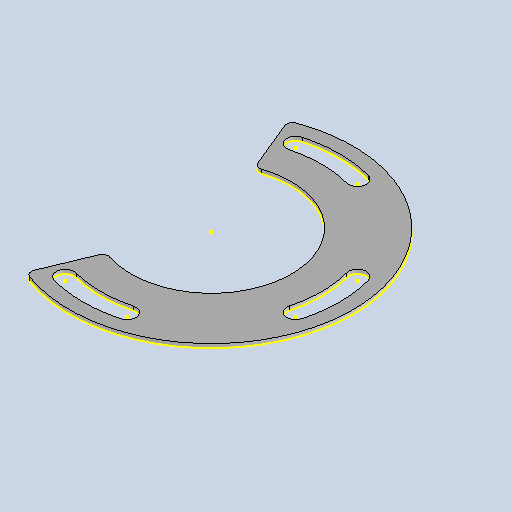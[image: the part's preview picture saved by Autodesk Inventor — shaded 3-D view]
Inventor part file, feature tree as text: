
AUTODESK INVENTOR PART (.ipt)
format: ipt  version: 2025.3 (Build 293356030, 356C)  size: 247,808 bytes
history: native  units: mm
features: sketch x3, other x3, sheet_metal_op x1, pattern_circular x1, chamfer x1, projected_geometry x1
ambient origin geometry x8: Origin, YZ Plane, XZ Plane, XY Plane, X Axis, Y Axis, Z Axis, Center Point
bodies: Body1 (feature_tree)
feature tree (10):
  sheet_metal_op  "Face2"
  pattern_circular  "Circular Pattern1"  Count=4 Angle=360.0deg
  chamfer  "Corner Round1"
  sketch  "Sketch5"  dims[d18=0.0mm d19=40.0mm d20=360.0deg d25=161.0mm d27=285.0mm d28=240.0mm d29=135.0deg d30=18.0mm d31=30.0deg d32=6.0mm]
  sketch  "Sketch2"  dims[d14=4.0mm]
  other  "Plate2"
  sketch  "Sketch3"  dims[d17=4.0mm]
  projected_geometry  "Projected Loop1"
  other  "Cut1"
  other  "Definition1"
